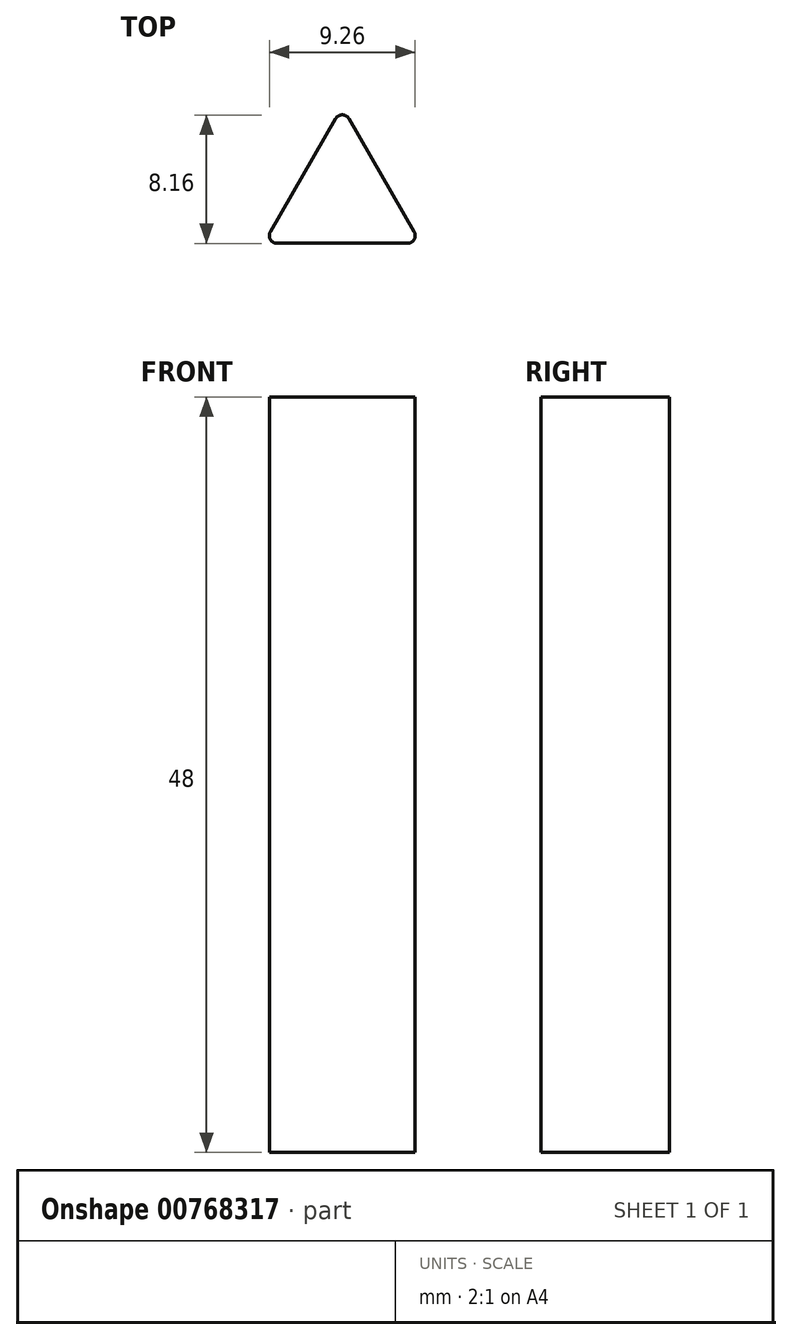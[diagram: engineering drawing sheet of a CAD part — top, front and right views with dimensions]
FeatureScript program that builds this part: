
annotation { "Feature Type Name" : "Feature", "Feature Type Description" : "" }
export const myFeature = defineFeature(function(context is Context, id is Id, definition is map)
    precondition{}
    {
        {
            var Q0;
            Q0=qCreatedBy(makeId("Top.planeOp"),FACE);
            var sketch = newSketch(context, id + "F0", { "sketchPlane" : qUnion([Q0])});
            skCircle(sketch, "E0.cCircle", {"center": v(0, 0) * mm, "radius": 5.77 * mm, "construction": true});
            skLineSegment(sketch, "E0.0", {"start": v(0.43, 5.02) * mm, "end": v(4.57, -2.14) * mm});
            skLineSegment(sketch, "E0.1", {"start": v(4.13, -2.89) * mm, "end": v(-4.13, -2.89) * mm});
            skLineSegment(sketch, "E0.2", {"start": v(-4.57, -2.14) * mm, "end": v(-0.43, 5.02) * mm});
            skPoint(sketch, "E1.visualSharp", {"position": v(0, 5.77) * mm});
            skArc(sketch, "E1.filletArc", {"start": v(0.43, 5.02) * mm, "mid": v(0, 5.27) * mm, "end": v(-0.43, 5.02) * mm});
            skPoint(sketch, "E2.visualSharp", {"position": v(-5, -2.89) * mm});
            skArc(sketch, "E2.filletArc", {"start": v(-4.57, -2.14) * mm, "mid": v(-4.57, -2.64) * mm, "end": v(-4.13, -2.89) * mm});
            skPoint(sketch, "E3.visualSharp", {"position": v(5, -2.89) * mm});
            skArc(sketch, "E3.filletArc", {"start": v(4.13, -2.89) * mm, "mid": v(4.57, -2.64) * mm, "end": v(4.57, -2.14) * mm});
            skSolve(sketch);
        }
        {
            var Q0;
            Q0=makeQuery(id+"F0.imprint","IMPRINT",FACE,{"disambiguationData":[TD([[makeQuery(id+"F0.imprint","IMPRINT",EDGE,{"derivedFrom":sQuery(id+"F0.wireOp",EDGE,"E0.0")}),-1.0]])]});
            extrude(context, id + "F1", {"entities" : qUnion([Q0]), "depth" : 48 * mm, "offsetDistance" : 25 * mm});
        }
    });
